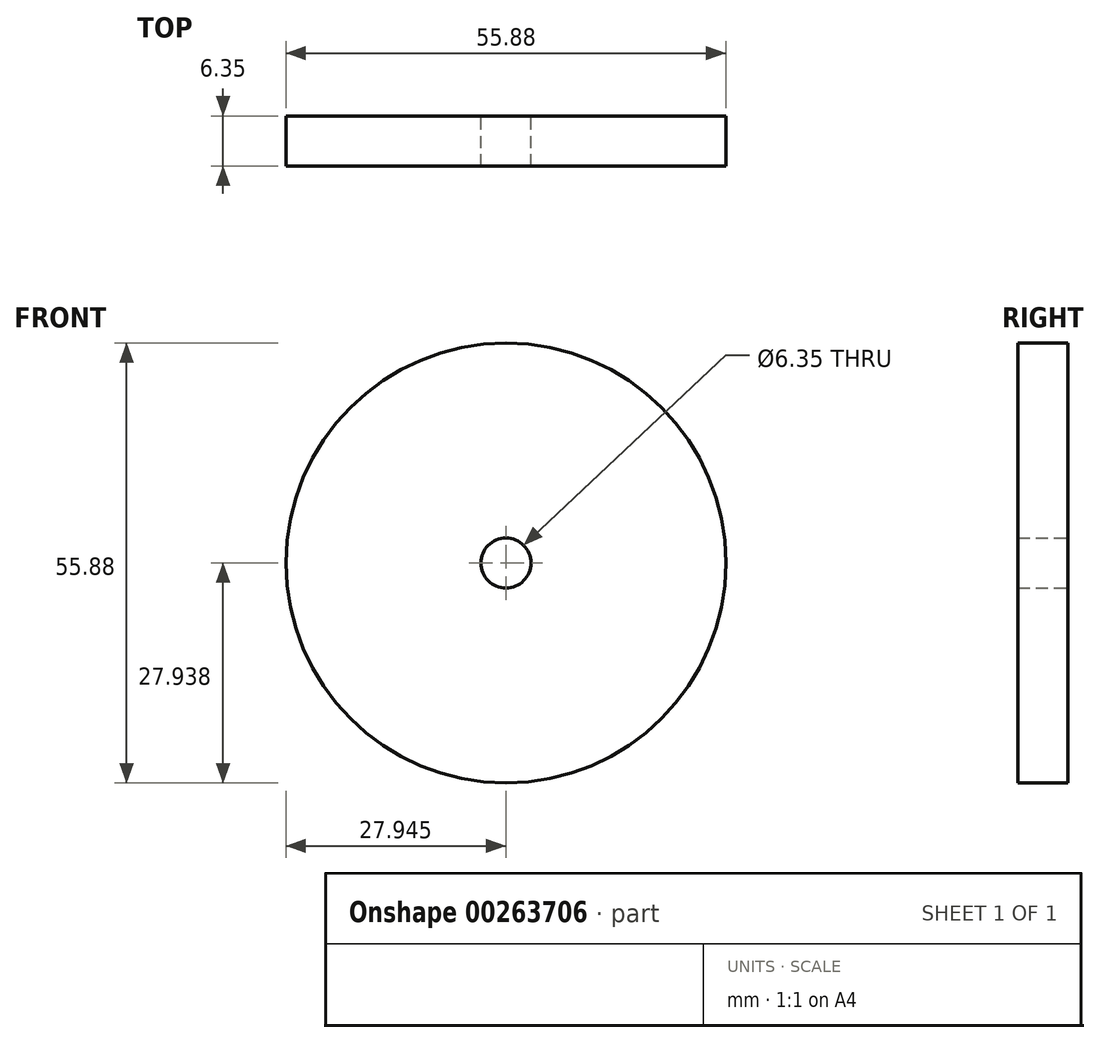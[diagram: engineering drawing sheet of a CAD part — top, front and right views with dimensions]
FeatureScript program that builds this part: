
annotation { "Feature Type Name" : "Feature", "Feature Type Description" : "" }
export const myFeature = defineFeature(function(context is Context, id is Id, definition is map)
    precondition{}
    {
        {
            var Q0;
            Q0=qCreatedBy(makeId("Front.planeOp"),FACE);
            var sketch = newSketch(context, id + "F0", { "sketchPlane" : qUnion([Q0])});
            skCircle(sketch, "E0", {"center": v(57.74, 69.22) * mm, "radius": 27.94 * mm});
            skCircle(sketch, "E1", {"center": v(57.74, 69.22) * mm, "radius": 3.18 * mm});
            skSolve(sketch);
        }
        {
            var Q0;
            Q0=makeQuery(id+"F0.imprint","IMPRINT",FACE,{"disambiguationData":[TD([[makeQuery(id+"F0.imprint","IMPRINT",EDGE,{"derivedFrom":sQuery(id+"F0.wireOp",EDGE,"E0")}),1.0]])]});
            extrude(context, id + "F1", {"entities" : qUnion([Q0]), "depth" : 6.35 * mm});
        }
    });
